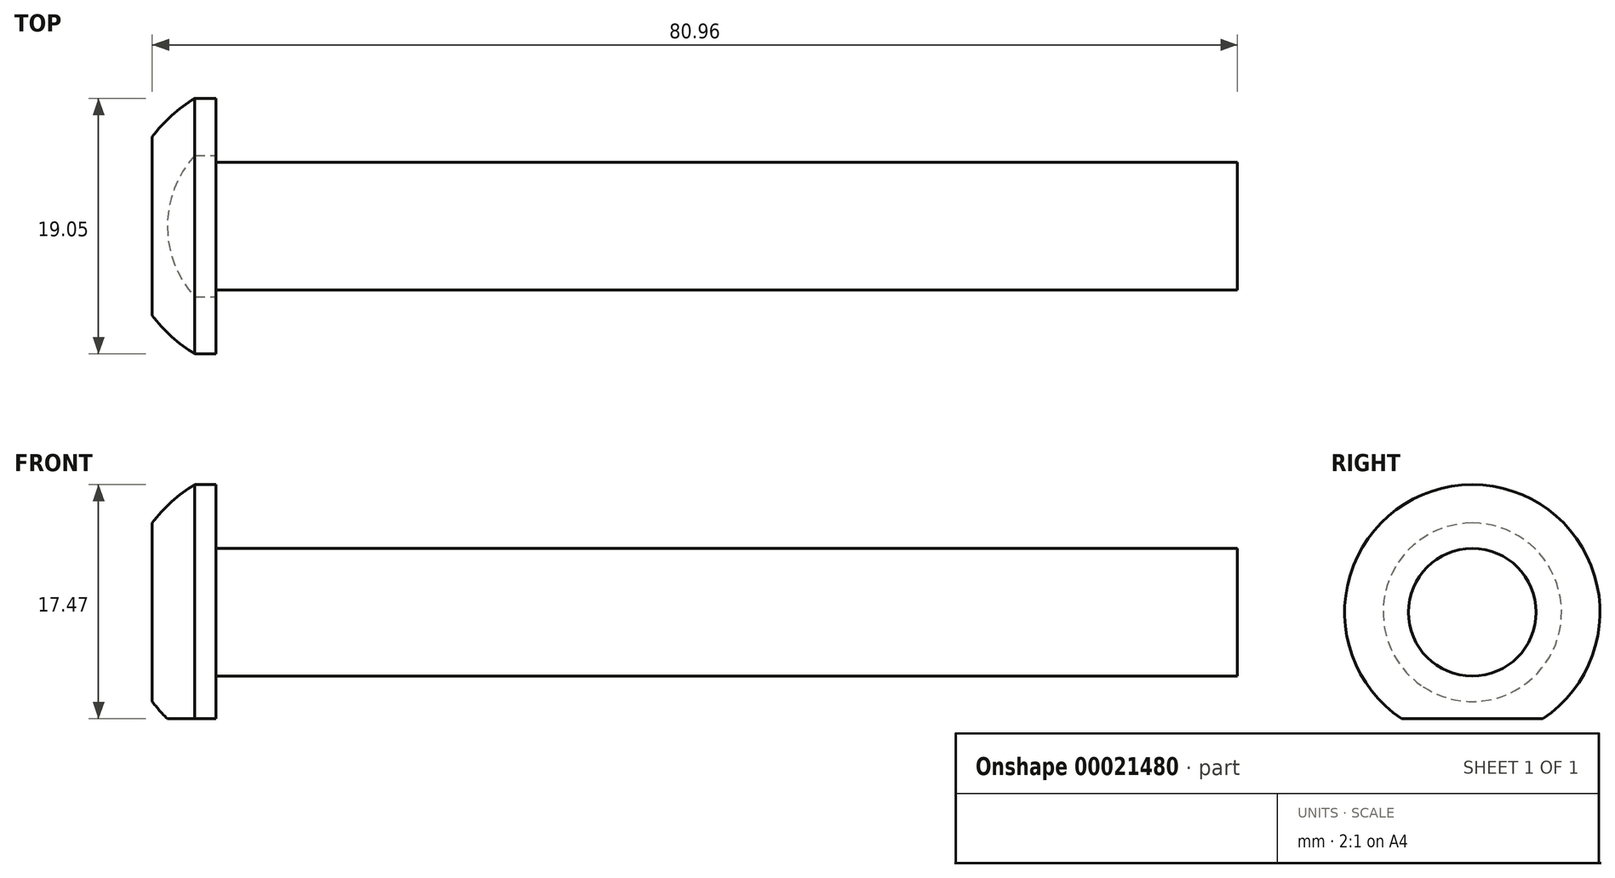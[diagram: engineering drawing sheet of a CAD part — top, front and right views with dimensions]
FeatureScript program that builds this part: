
annotation { "Feature Type Name" : "Feature", "Feature Type Description" : "" }
export const myFeature = defineFeature(function(context is Context, id is Id, definition is map)
    precondition{}
    {
        {
            var Q0;
            Q0=qCreatedBy(makeId("Top.planeOp"),FACE);
            var sketch = newSketch(context, id + "F0", { "sketchPlane" : qUnion([Q0])});
            skLineSegment(sketch, "E0.top", {"start": v(3.18, -11.11) * mm, "end": v(4.76, -11.11) * mm});
            skLineSegment(sketch, "E0.left", {"start": v(0, -1.59) * mm, "end": v(0, -8.24) * mm});
            skLineSegment(sketch, "E0.right", {"start": v(4.76, -6.35) * mm, "end": v(4.76, -11.11) * mm});
            skArc(sketch, "E1", {"start": v(0, -8.24) * mm, "mid": v(1.45, -9.83) * mm, "end": v(3.17, -11.11) * mm});
            skLineSegment(sketch, "E2", {"start": v(0, -1.59) * mm, "end": v(4.76, -1.59) * mm});
            skLineSegment(sketch, "E3.bottom", {"start": v(4.76, -1.59) * mm, "end": v(80.96, -1.59) * mm});
            skLineSegment(sketch, "E3.top", {"start": v(4.76, -6.35) * mm, "end": v(80.96, -6.35) * mm});
            skLineSegment(sketch, "E3.right", {"start": v(80.96, -1.59) * mm, "end": v(80.96, -6.35) * mm});
            skSolve(sketch);
        }
        {
            var Q0;
            Q0=makeQuery(id+"F0.imprint","IMPRINT",FACE,{"disambiguationData":[TD([[makeQuery(id+"F0.imprint","IMPRINT",EDGE,{"derivedFrom":sQuery(id+"F0.wireOp",EDGE,"E0.top")}),1.0]])]});
            var Q1;
            Q1=sQuery(id+"F0.wireOp",EDGE,"E3.bottom");
            revolve(context, id + "F1", {"entities" : qUnion([Q0]), "axis" : qUnion([Q1]), "revolveType" : RevolveType.FULL});
        }
        {
            var Q0;
            Q0=makeQuery(id+"F1.opRevolve","SWEPT_FACE",FACE,{"disambiguationData":[OSD([sQuery(id+"F0.wireOp",EDGE,"E0.right")])]});
            var sketch = newSketch(context, id + "F2", { "sketchPlane" : qUnion([Q0])});
            skLineSegment(sketch, "E4.bottom", {"start": v(9.69, -7.94) * mm, "end": v(-13.29, -7.94) * mm});
            skLineSegment(sketch, "E4.top", {"start": v(9.69, -14.85) * mm, "end": v(-13.29, -14.85) * mm});
            skLineSegment(sketch, "E4.left", {"start": v(9.69, -7.94) * mm, "end": v(9.69, -14.85) * mm});
            skLineSegment(sketch, "E4.right", {"start": v(-13.29, -7.94) * mm, "end": v(-13.29, -14.85) * mm});
            skCircle(sketch, "E5.0", {"center": v(-1.59, 0) * mm, "radius": 4.76 * mm});
            skSolve(sketch);
        }
        {
            var Q0;
            {var subQ0=makeQuery(id+"F1.opRevolve","SWEPT_EDGE",EDGE,{"disambiguationData":[OSD([sQuery(id+"F0.wireOp",EDGE,"E0.top"),sQuery(id+"F0.wireOp",EDGE,"E0.right")])]});var subQ1=sQuery(id+"F2.wireOp",EDGE,"E4.bottom");var subQ3=makeQuery(id+"F2.imprint","INTERSECT",VERTEX,{"disambiguationData":[OD(0.0)],"derivedFrom":[subQ0,subQ1]});Q0=makeQuery(id+"F2.imprint","IMPRINT",FACE,{"disambiguationData":[TD([[makeQuery(id+"F2.imprint","IMPRINT",EDGE,{"disambiguationData":[TD([[subQ3,-1.0]])],"derivedFrom":subQ1}),1.0]])]});}
            extrude(context, id + "F3", {"entities" : qUnion([Q0]), "operationType" : NewBodyOperationType.REMOVE, "oppositeDirection" : true, "depth" : 25.4 * mm});
        }
    });
